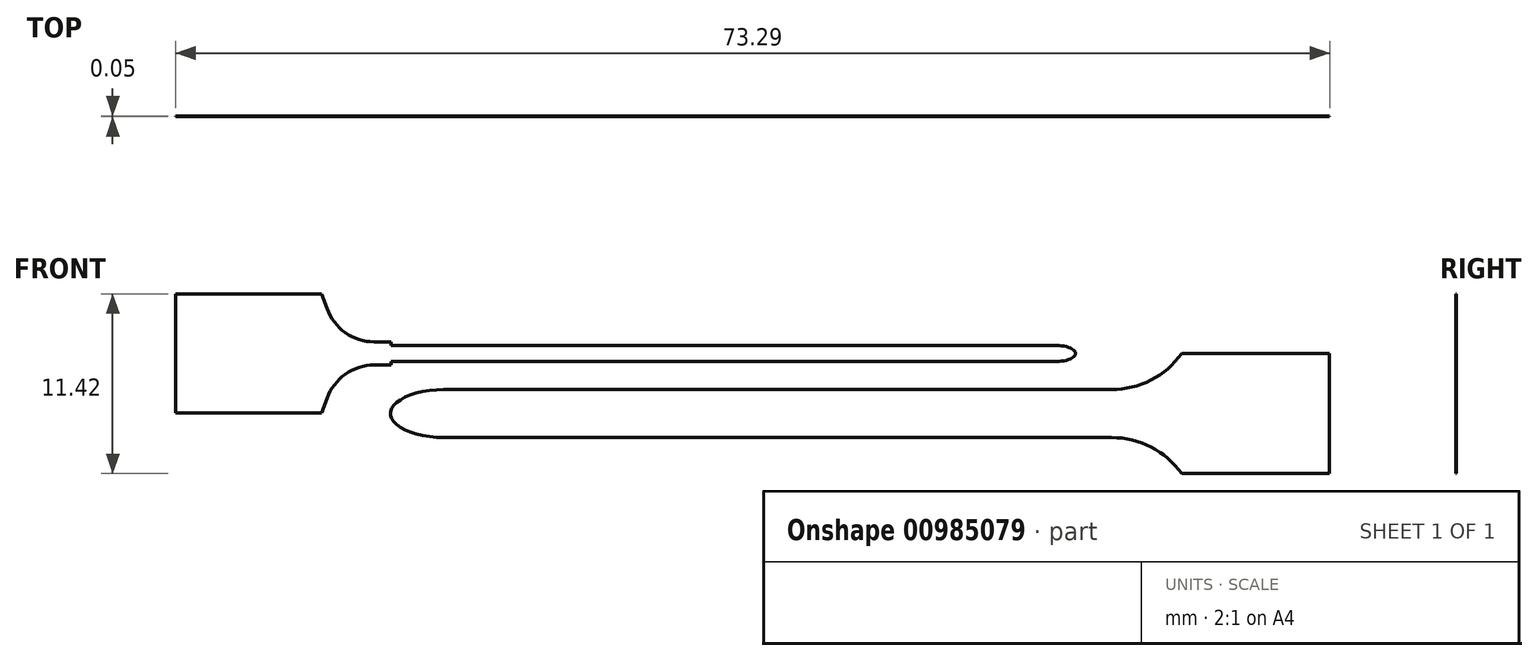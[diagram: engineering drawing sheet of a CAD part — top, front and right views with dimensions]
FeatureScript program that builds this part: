
annotation { "Feature Type Name" : "Feature", "Feature Type Description" : "" }
export const myFeature = defineFeature(function(context is Context, id is Id, definition is map)
    precondition{}
    {
        {
            var Q0;
            Q0=qCreatedBy(makeId("Front.planeOp"),FACE);
            var sketch = newSketch(context, id + "F0", { "sketchPlane" : qUnion([Q0])});
            skLineSegment(sketch, "E0.0.0", {"start": v(-31.53, 2.72) * mm, "end": v(-31.53, -4.85) * mm});
            skLineSegment(sketch, "E0.0.1", {"start": v(-31.53, -4.85) * mm, "end": v(-22.25, -4.85) * mm});
            skLineSegment(sketch, "E0.0.2", {"start": v(-22.25, -4.85) * mm, "end": v(-21.92, -3.92) * mm});
            skArc(sketch, "E0.0.3", {"start": v(-21.92, -3.92) * mm, "mid": v(-20.76, -2.39) * mm, "end": v(-18.93, -1.8) * mm});
            skLineSegment(sketch, "E0.0.4", {"start": v(-18.93, -1.8) * mm, "end": v(-17.85, -1.8) * mm});
            skLineSegment(sketch, "E0.0.5", {"start": v(-17.85, -1.8) * mm, "end": v(-17.85, -1.58) * mm});
            skLineSegment(sketch, "E0.0.6", {"start": v(-17.85, -1.58) * mm, "end": v(24.4, -1.58) * mm});
            skLineSegment(sketch, "E0.0.8", {"start": v(24.4, -0.56) * mm, "end": v(-17.85, -0.56) * mm});
            skLineSegment(sketch, "E0.0.9", {"start": v(-17.85, -0.56) * mm, "end": v(-17.85, -0.33) * mm});
            skLineSegment(sketch, "E0.0.10", {"start": v(-17.85, -0.33) * mm, "end": v(-18.93, -0.33) * mm});
            skArc(sketch, "E0.0.11", {"start": v(-18.93, -0.33) * mm, "mid": v(-20.76, 0.25) * mm, "end": v(-21.92, 1.78) * mm});
            skLineSegment(sketch, "E0.0.12", {"start": v(-21.92, 1.78) * mm, "end": v(-22.25, 2.72) * mm});
            skLineSegment(sketch, "E0.0.13", {"start": v(-22.25, 2.72) * mm, "end": v(-31.53, 2.72) * mm});
            skLineSegment(sketch, "E1", {"start": v(25.62, -1.07) * mm, "end": v(25.62, -0.28) * mm, "construction": true});
            skLineSegment(sketch, "E2", {"start": v(24.4, -1.58) * mm, "end": v(24.4, -0.56) * mm, "construction": true});
            skLineSegment(sketch, "E3", {"start": v(-31.53, -1.07) * mm, "end": v(-31.53, 12.08) * mm, "construction": true});
            skLineSegment(sketch, "E4", {"start": v(-31.53, -1.07) * mm, "end": v(27.36, -1.07) * mm, "construction": true});
            skEllipticalArc(sketch, "E5", {});
            const initialGuessF0  = {"E5": [0.024399346867346877, -0.0010696597954883004, 1, 0, 0.0012249929191943676, 0.0005079969175384095, 4.71238898038469, 1.5707963267948961]};
            skSetInitialGuess(sketch, initialGuessF0);
            skSolve(sketch);
        }
        {
            var Q0;
            Q0=qCreatedBy(makeId("Front.planeOp"),FACE);
            var sketch = newSketch(context, id + "F1", { "sketchPlane" : qUnion([Q0])});
            skLineSegment(sketch, "E6", {"start": v(-14.5, -3.36) * mm, "end": v(-14.96, -3.38) * mm});
            skLineSegment(sketch, "E7", {"start": v(-14.96, -3.38) * mm, "end": v(-15.42, -3.42) * mm});
            skLineSegment(sketch, "E8", {"start": v(-15.42, -3.42) * mm, "end": v(-15.85, -3.49) * mm});
            skLineSegment(sketch, "E9", {"start": v(-15.85, -3.49) * mm, "end": v(-16.26, -3.58) * mm});
            skLineSegment(sketch, "E10", {"start": v(-16.26, -3.58) * mm, "end": v(-16.64, -3.7) * mm});
            skLineSegment(sketch, "E11", {"start": v(-16.64, -3.7) * mm, "end": v(-16.98, -3.85) * mm});
            skLineSegment(sketch, "E12", {"start": v(-16.98, -3.85) * mm, "end": v(-17.27, -4) * mm});
            skLineSegment(sketch, "E13", {"start": v(-17.27, -4) * mm, "end": v(-17.5, -4.19) * mm});
            skLineSegment(sketch, "E14", {"start": v(-17.5, -4.19) * mm, "end": v(-17.7, -4.38) * mm});
            skLineSegment(sketch, "E15", {"start": v(-17.7, -4.38) * mm, "end": v(-17.81, -4.58) * mm});
            skLineSegment(sketch, "E16", {"start": v(-17.81, -4.58) * mm, "end": v(-17.88, -4.78) * mm});
            skLineSegment(sketch, "E17", {"start": v(-17.88, -4.78) * mm, "end": v(-17.88, -5) * mm});
            skLineSegment(sketch, "E18", {"start": v(-17.88, -5) * mm, "end": v(-17.81, -5.2) * mm});
            skLineSegment(sketch, "E19", {"start": v(-17.81, -5.2) * mm, "end": v(-17.7, -5.4) * mm});
            skLineSegment(sketch, "E20", {"start": v(-17.7, -5.4) * mm, "end": v(-17.5, -5.59) * mm});
            skLineSegment(sketch, "E21", {"start": v(-17.5, -5.59) * mm, "end": v(-17.27, -5.77) * mm});
            skLineSegment(sketch, "E22", {"start": v(-17.27, -5.77) * mm, "end": v(-16.98, -5.93) * mm});
            skLineSegment(sketch, "E23", {"start": v(-16.98, -5.93) * mm, "end": v(-16.64, -6.07) * mm});
            skLineSegment(sketch, "E24", {"start": v(-16.64, -6.07) * mm, "end": v(-16.26, -6.19) * mm});
            skLineSegment(sketch, "E25", {"start": v(-16.26, -6.19) * mm, "end": v(-15.85, -6.28) * mm});
            skLineSegment(sketch, "E26", {"start": v(-15.85, -6.28) * mm, "end": v(-15.42, -6.35) * mm});
            skLineSegment(sketch, "E27", {"start": v(-15.42, -6.35) * mm, "end": v(-14.96, -6.4) * mm});
            skLineSegment(sketch, "E28", {"start": v(-14.96, -6.4) * mm, "end": v(-14.5, -6.41) * mm});
            skLineSegment(sketch, "E29", {"start": v(27.91, -3.36) * mm, "end": v(-14.5, -3.36) * mm});
            skLineSegment(sketch, "E30", {"start": v(41.76, -1.08) * mm, "end": v(32.36, -1.08) * mm});
            skLineSegment(sketch, "E31", {"start": v(41.76, -8.7) * mm, "end": v(41.76, -1.08) * mm});
            skLineSegment(sketch, "E32", {"start": v(32.36, -8.7) * mm, "end": v(41.76, -8.7) * mm});
            skLineSegment(sketch, "E33", {"start": v(-14.5, -6.41) * mm, "end": v(27.91, -6.41) * mm});
            skArc(sketch, "E34", {"start": v(27.91, -3.36) * mm, "mid": v(30.41, -2.76) * mm, "end": v(32.36, -1.08) * mm});
            skArc(sketch, "E35", {"start": v(32.36, -8.7) * mm, "mid": v(30.41, -7.02) * mm, "end": v(27.91, -6.41) * mm});
            skSolve(sketch);
        }
        {
            var Q0;
            Q0=makeQuery(id+"F0.imprint","IMPRINT",FACE,{"disambiguationData":[TD([[makeQuery(id+"F0.imprint","IMPRINT",EDGE,{"derivedFrom":sQuery(id+"F0.wireOp",EDGE,"E0.0.0")}),1.0]])]});
            var Q1;
            Q1=makeQuery(id+"F1.imprint","IMPRINT",FACE,{"disambiguationData":[TD([[makeQuery(id+"F1.imprint","IMPRINT",EDGE,{"derivedFrom":sQuery(id+"F1.wireOp",EDGE,"E6")}),1.0]])]});
            extrude(context, id + "F2", {"entities" : qUnion([Q0, Q1]), "depth" : 0.05 * mm, "offsetDistance" : 25.4 * mm});
        }
    });
